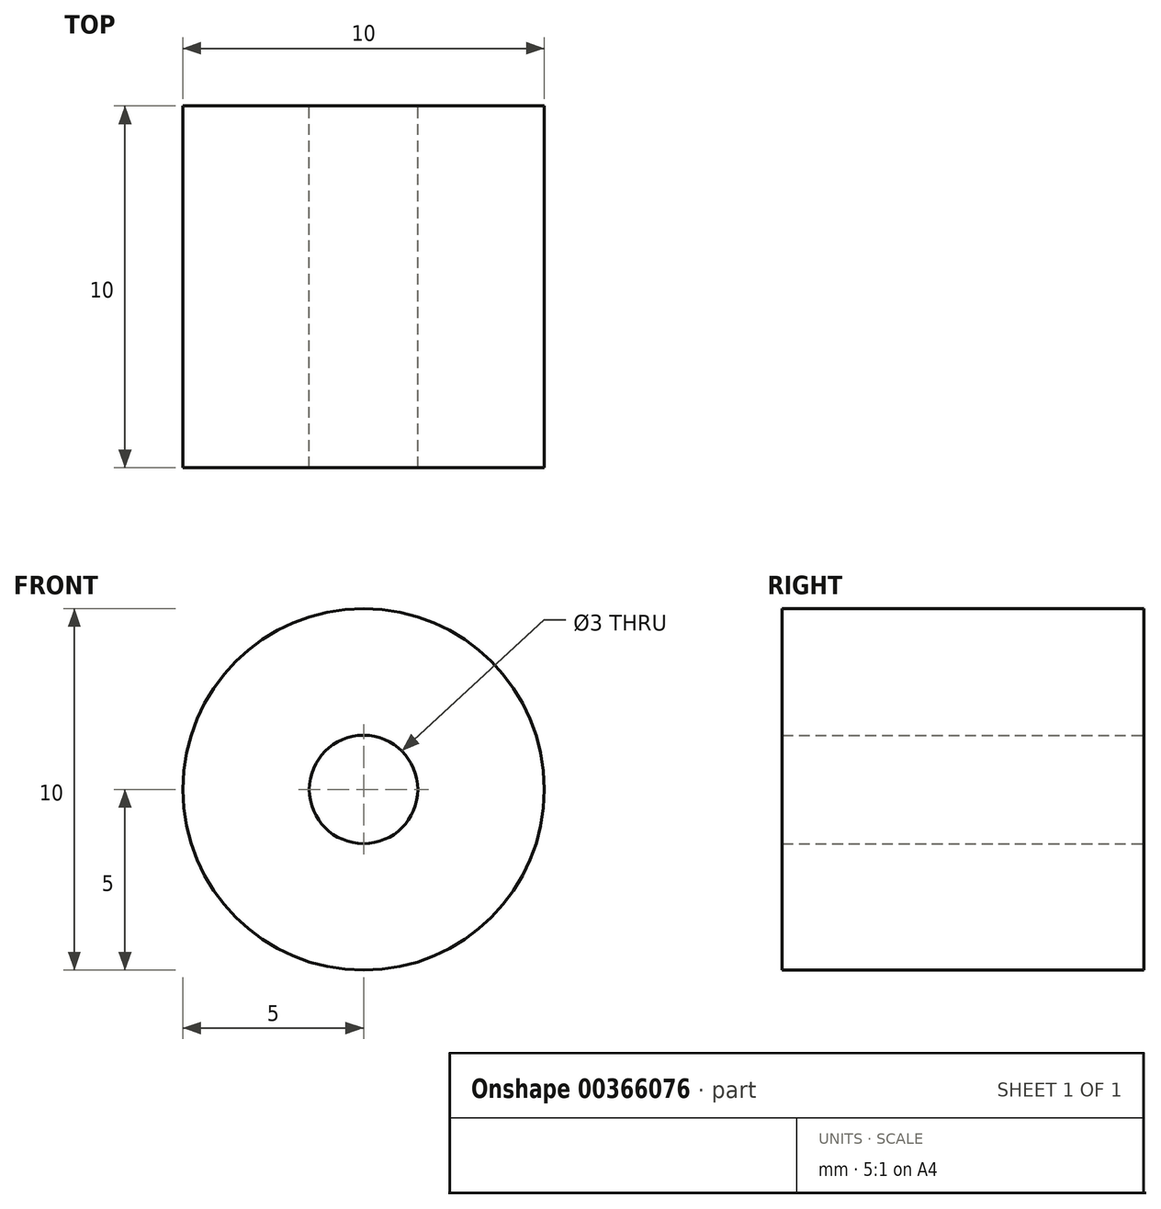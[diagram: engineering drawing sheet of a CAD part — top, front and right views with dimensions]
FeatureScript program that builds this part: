
annotation { "Feature Type Name" : "Feature", "Feature Type Description" : "" }
export const myFeature = defineFeature(function(context is Context, id is Id, definition is map)
    precondition{}
    {
        {
            var Q0;
            Q0=qCreatedBy(makeId("Front.planeOp"),FACE);
            var sketch = newSketch(context, id + "F0", { "sketchPlane" : qUnion([Q0])});
            skCircle(sketch, "E0", {"center": v(0, 0) * mm, "radius": 5 * mm});
            skCircle(sketch, "E1", {"center": v(0, 0) * mm, "radius": 1.5 * mm});
            skSolve(sketch);
        }
        {
            var Q0;
            Q0 = qSketchRegion(id + "F0", true);
            extrude(context, id + "F1", {"entities" : qUnion([Q0]), "depth" : 10 * mm});
        }
    });
